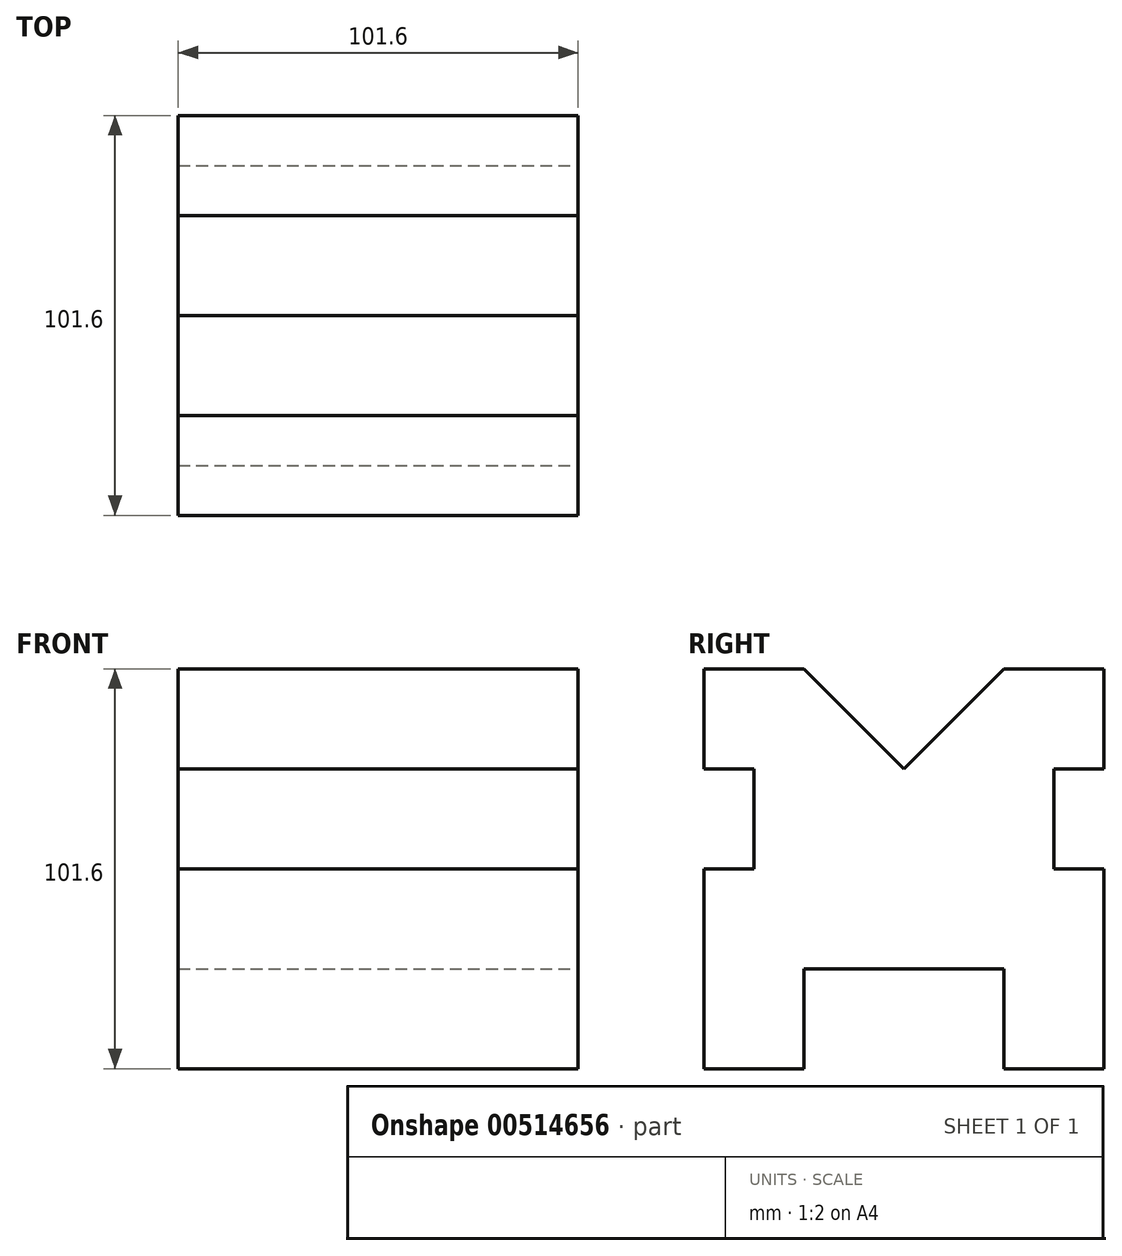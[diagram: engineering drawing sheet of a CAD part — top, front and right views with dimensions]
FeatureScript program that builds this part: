
annotation { "Feature Type Name" : "Feature", "Feature Type Description" : "" }
export const myFeature = defineFeature(function(context is Context, id is Id, definition is map)
    precondition{}
    {
        {
            var Q0;
            Q0=qCreatedBy(makeId("Front.planeOp"),FACE);
            var sketch = newSketch(context, id + "F0", { "sketchPlane" : qUnion([Q0])});
            skLineSegment(sketch, "E0", {"start": v(0, 0) * mm, "end": v(0, 101.6) * mm});
            skLineSegment(sketch, "E1", {"start": v(0, 101.6) * mm, "end": v(101.6, 101.6) * mm});
            skLineSegment(sketch, "E2", {"start": v(101.6, 101.6) * mm, "end": v(101.6, 0) * mm});
            skLineSegment(sketch, "E3", {"start": v(101.6, 0) * mm, "end": v(0, 0) * mm});
            skSolve(sketch);
        }
        {
            var Q0;
            Q0=makeQuery(id+"F0.imprint","IMPRINT",FACE,{"disambiguationData":[TD([[makeQuery(id+"F0.imprint","IMPRINT",EDGE,{"derivedFrom":sQuery(id+"F0.wireOp",EDGE,"E0")}),-1.0]])]});
            extrude(context, id + "F1", {"entities" : qUnion([Q0]), "oppositeDirection" : true, "depth" : 101.6 * mm, "offsetDistance" : 25.4 * mm});
        }
        {
            var Q0;
            Q0=makeQuery(id+"F1.opExtrude","SWEPT_FACE",FACE,{"disambiguationData":[OSD([sQuery(id+"F0.wireOp",EDGE,"E2")])]});
            var sketch = newSketch(context, id + "F2", { "sketchPlane" : qUnion([Q0])});
            skLineSegment(sketch, "E4", {"start": v(0, 0) * mm, "end": v(0, 50.8) * mm});
            skLineSegment(sketch, "E5", {"start": v(0, 50.8) * mm, "end": v(12.7, 50.8) * mm});
            skLineSegment(sketch, "E6", {"start": v(12.7, 50.8) * mm, "end": v(12.7, 76.2) * mm});
            skLineSegment(sketch, "E7", {"start": v(12.7, 76.2) * mm, "end": v(0, 76.2) * mm});
            skSolve(sketch);
        }
        {
            var Q0;
            {var subQ0=sQuery(id+"F2.wireOp",EDGE,"E5");Q0=makeQuery(id+"F2.imprint","IMPRINT",FACE,{"disambiguationData":[TD([[makeQuery(id+"F2.imprint","IMPRINT",EDGE,{"derivedFrom":subQ0}),1.0]])]});}
            extrude(context, id + "F3", {"entities" : qUnion([Q0]), "operationType" : NewBodyOperationType.REMOVE, "oppositeDirection" : true, "depth" : 101.6 * mm, "offsetDistance" : 25.4 * mm});
        }
        {
            var Q0;
            Q0=makeQuery(id+"F1.opExtrude","SWEPT_FACE",FACE,{"disambiguationData":[OSD([sQuery(id+"F0.wireOp",EDGE,"E2")])]});
            var sketch = newSketch(context, id + "F4", { "sketchPlane" : qUnion([Q0])});
            skLineSegment(sketch, "E8", {"start": v(101.6, 0) * mm, "end": v(101.6, 50.8) * mm});
            skLineSegment(sketch, "E9", {"start": v(101.6, 50.8) * mm, "end": v(88.9, 50.8) * mm});
            skLineSegment(sketch, "E10", {"start": v(88.9, 50.8) * mm, "end": v(88.9, 76.2) * mm});
            skLineSegment(sketch, "E11", {"start": v(88.9, 76.2) * mm, "end": v(101.6, 76.2) * mm});
            skSolve(sketch);
        }
        {
            var Q0;
            {var subQ0=sQuery(id+"F4.wireOp",EDGE,"E9");Q0=makeQuery(id+"F4.imprint","IMPRINT",FACE,{"disambiguationData":[TD([[makeQuery(id+"F4.imprint","IMPRINT",EDGE,{"derivedFrom":subQ0}),-1.0]])]});}
            extrude(context, id + "F5", {"entities" : qUnion([Q0]), "operationType" : NewBodyOperationType.REMOVE, "oppositeDirection" : true, "depth" : 101.6 * mm, "offsetDistance" : 25.4 * mm});
        }
        {
            var Q0;
            Q0=makeQuery(id+"F1.opExtrude","SWEPT_FACE",FACE,{"disambiguationData":[OSD([sQuery(id+"F0.wireOp",EDGE,"E2")])]});
            var sketch = newSketch(context, id + "F6", { "sketchPlane" : qUnion([Q0])});
            skLineSegment(sketch, "E12", {"start": v(0, 0) * mm, "end": v(25.4, 0) * mm});
            skLineSegment(sketch, "E13", {"start": v(25.4, 0) * mm, "end": v(25.4, 25.4) * mm});
            skLineSegment(sketch, "E14", {"start": v(25.4, 25.4) * mm, "end": v(76.2, 25.4) * mm});
            skLineSegment(sketch, "E15", {"start": v(76.2, 25.4) * mm, "end": v(76.2, 0) * mm});
            skSolve(sketch);
        }
        {
            var Q0;
            {var subQ0=sQuery(id+"F6.wireOp",EDGE,"E13");Q0=makeQuery(id+"F6.imprint","IMPRINT",FACE,{"disambiguationData":[TD([[makeQuery(id+"F6.imprint","IMPRINT",EDGE,{"derivedFrom":subQ0}),-1.0]])]});}
            extrude(context, id + "F7", {"entities" : qUnion([Q0]), "operationType" : NewBodyOperationType.REMOVE, "oppositeDirection" : true, "depth" : 101.6 * mm, "offsetDistance" : 25.4 * mm});
        }
        {
            var Q0;
            Q0=makeQuery(id+"F1.opExtrude","SWEPT_FACE",FACE,{"disambiguationData":[OSD([sQuery(id+"F0.wireOp",EDGE,"E2")])]});
            var sketch = newSketch(context, id + "F8", { "sketchPlane" : qUnion([Q0])});
            skLineSegment(sketch, "E16", {"start": v(0, 101.6) * mm, "end": v(25.4, 101.6) * mm});
            skLineSegment(sketch, "E17", {"start": v(101.6, 101.6) * mm, "end": v(76.2, 101.6) * mm});
            skLineSegment(sketch, "E18", {"start": v(76.2, 101.6) * mm, "end": v(50.8, 101.6) * mm});
            skLineSegment(sketch, "E19", {"start": v(50.8, 101.6) * mm, "end": v(50.8, 76.2) * mm});
            skLineSegment(sketch, "E20", {"start": v(50.8, 76.2) * mm, "end": v(25.4, 101.6) * mm});
            skLineSegment(sketch, "E21", {"start": v(50.8, 76.2) * mm, "end": v(76.2, 101.6) * mm});
            skSolve(sketch);
        }
        {
            var Q0;
            {var subQ0=sQuery(id+"F8.wireOp",EDGE,"E19");Q0=makeQuery(id+"F8.imprint","IMPRINT",FACE,{"disambiguationData":[TD([[makeQuery(id+"F8.imprint","IMPRINT",EDGE,{"derivedFrom":subQ0}),-1.0]])]});}
            var Q1;
            Q1=makeQuery(id+"F8.imprint","IMPRINT",FACE,{"disambiguationData":[TD([[makeQuery(id+"F8.imprint","IMPRINT",EDGE,{"derivedFrom":sQuery(id+"F8.wireOp",EDGE,"E18")}),1.0]])]});
            extrude(context, id + "F9", {"entities" : qUnion([Q0, Q1]), "operationType" : NewBodyOperationType.REMOVE, "oppositeDirection" : true, "depth" : 101.6 * mm, "offsetDistance" : 25.4 * mm});
        }
    });
